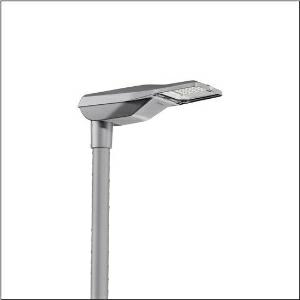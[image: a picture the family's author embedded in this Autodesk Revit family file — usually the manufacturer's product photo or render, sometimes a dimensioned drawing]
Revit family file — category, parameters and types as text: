
# Revit family: streetlight_sl_21_iq_micro___p0_8ab_5xe1r31g08db_e4e9
name_source: partatom
category: Lighting Fixtures
units: mm (PartAtom-declared; Revit-internal decimal feet)

## family parameters
Cut with Voids When Loaded = No
Host = Face
Light Source = No
Part Type = Normal
Room Calculation Point = No
Round Connector Dimension = Use Diameter
Shared = No

## types (1)
- --- (1 x LED, 4220 lm, 36.4 W, 3000K)
    Apparent Load = 36 VA
    CIE Flux Codes = 36 71 98 100 100
    Color Rendering = 70
    Color Temperature = 3000K
    Default Elevation = 1800 mm
    Description = Streetlight SL 21 iQ micro, mast luminaire, primary light control with lens, of PMMA, primary optical cover: cover, of toughened safety glass, transparent, light distribution: P0.8aB, light emission: direct distribution, primary light characteristic: asymmetric, installation type: post-top, side-entry, LED, High Power LED, rated luminous flux: 4.220lm, luminous efficacy: 116lm/W, light colour: 730, colour temperature: 3000K, control gear: iQ Street-Remote, control: pre-setting: linear dimming characteristic, Street-Remote, Auto-Match, Temp-Guard, Lumen-Switch, Night-Set, Smart-Wire, Light-Fading, Desk-Remote (wireless, voltage-free reading and setting of iQ features in the workshop via application-optimized NFC function/RFID function), optimised constant luminous flux control (CLO 2.0), mains connection: 220..240V, AC, 50/60Hz, start of lifetime: 36W, end of service life: 38W, reduction: 16W, luminaire housing, of diecast aluminium, powder-coated, Siteco® metallic grey (DB 702S), corrosivity category C5 mid according to DIN EN ISO 12944, please order mast flange separately, inclination adjustable: 0°, 5°, 10°, 15°, sealing non-destructively replaceable, multi-level sealing system, length: 528mm, width: 235mm, height: 110mm, mast flange for spigot size: 42mm (side-entry): 5XC10008XM4, 60/48mm (side-entry/post-top): 5XC10108XM2, 76/60mm (side-entry/post-top): 5XC10108XM1, protection rating (complete): IP66, insulation class (complete): insulation class II (safety insulation), certification: CE, ENEC, ENEC+, VDE, impact resistance: IK10, permissible operating ambient temperature for outdoor applications: -40..+50°C, standard-compliant lighting for roads and squares, packaging unit: 1 piece

Light Distribution: P0.8aB
    Height = 110 mm
    Lamp = 1 x LED
    Lamp Light Flux = 4220 lm
    Lamp Power = 36.4 W
    Lamp count = 1
    Length = 528 mm
    Luminous efficacy = 116 lm/W
    Manufacturer = Siteco
    ModVariant = No
    Model = 5XE1R31G08DB
    Number of Poles = 1
    OnlyDefault = Yes
    Power Factor = 1
    Product Name = Streetlight SL 21 iQ micro | P0.8aB
    Product group = mast luminaire | pylon top
    ProductGroupID = 6100
    Protection Class = Protection class II
    Protection Degree = IP 66
    RLX_Detail_Level = 1
    RLX_Emergency_Light_Flux = 0 lm
    RLX_Emergency_Type = 0
    RLX_Emergency_Type_DB = No
    RlxData = <blob elided: 99073 chars, md5=7b706da9>
    Socket = socket
    Standby Power = 0 W
    System Light Flux = 4220 lm
    System Power = 36 W
    Type Comments = factory setting: luminous flux: 100 % | dim-lin: 254 | 715 mA
    Type Image = l_1006881.jpg
    URL = http://relux.com
    VarID = @adj_074784
    Voltage = 0 V
    Weight = 0.00 kg
    Width = 235 mm

## geometry (parser evidence)
native form markers: Blend x4, Sweep x9
no freeform markers — native parametric forms only
